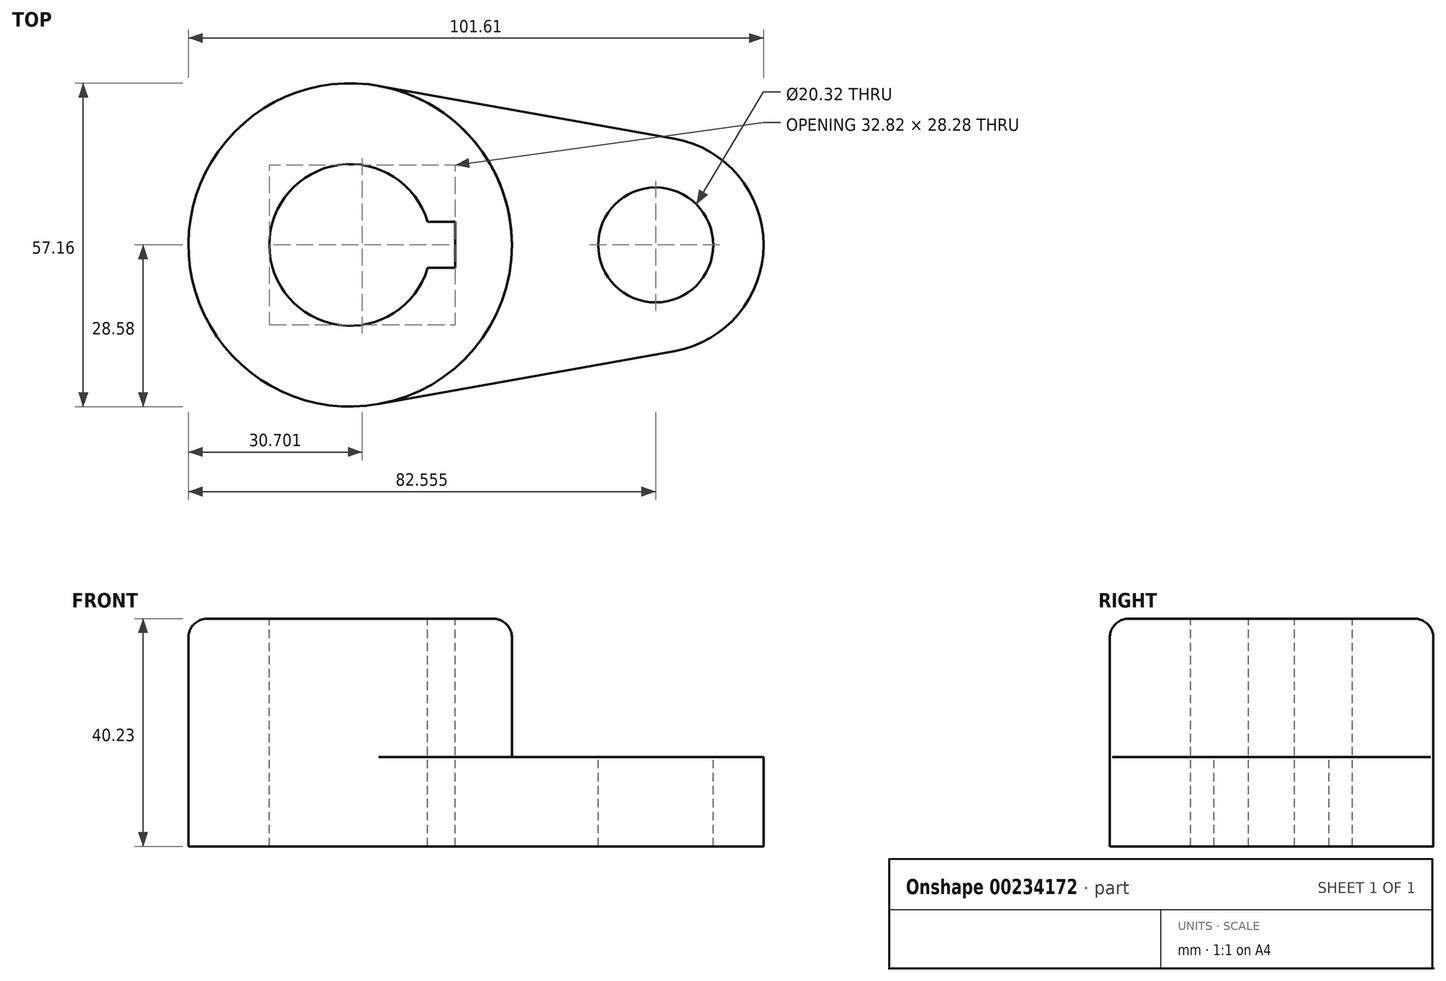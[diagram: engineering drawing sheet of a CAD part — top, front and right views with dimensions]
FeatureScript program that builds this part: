
annotation { "Feature Type Name" : "Feature", "Feature Type Description" : "" }
export const myFeature = defineFeature(function(context is Context, id is Id, definition is map)
    precondition{}
    {
        {
            var Q0;
            Q0=qCreatedBy(makeId("Top.planeOp"),FACE);
            var sketch = newSketch(context, id + "F0", { "sketchPlane" : qUnion([Q0])});
            skCircle(sketch, "E0", {"center": v(0, 0) * mm, "radius": 28.58 * mm});
            skSolve(sketch);
        }
        {
            var Q0;
            Q0=qSketchRegion(id+"F0",true);
            extrude(context, id + "F1", {"entities" : qUnion([Q0]), "depth" : 40.23 * mm});
        }
        {
            var Q0;
            Q0=qCreatedBy(makeId("Top.planeOp"),FACE);
            var sketch = newSketch(context, id + "F2", { "sketchPlane" : qUnion([Q0])});
            skLineSegment(sketch, "E1", {"start": v(53.98, 0) * mm, "end": v(53.98, -36.04) * mm, "construction": true});
            skLineSegment(sketch, "E2", {"start": v(53.98, -36.04) * mm, "end": v(53.98, 27.42) * mm, "construction": true});
            skArc(sketch, "E3", {"start": v(53.98, -19.05) * mm, "mid": v(73.03, 0) * mm, "end": v(53.98, 19.05) * mm});
            skLineSegment(sketch, "E4", {"start": v(5.04, -28.13) * mm, "end": v(57.34, -18.75) * mm});
            skArc(sketch, "E5", {"start": v(5.04, 28.13) * mm, "mid": v(-28.58, 0) * mm, "end": v(5.04, -28.13) * mm});
            skLineSegment(sketch, "E6", {"start": v(-19.16, 0) * mm, "end": v(100.57, 0) * mm, "construction": true});
            skLineSegment(sketch, "E7.MirrorCS", {"start": v(5.04, 28.13) * mm, "end": v(57.34, 18.75) * mm});
            skSolve(sketch);
        }
        {
            var Q0;
            Q0=qSketchRegion(id+"F2",true);
            extrude(context, id + "F3", {"entities" : qUnion([Q0]), "operationType" : NewBodyOperationType.ADD, "depth" : 15.77 * mm});
        }
        {
            var Q0;
            Q0=makeQuery(id+"F1.opExtrude","CAP_FACE",FACE,{"disambiguationData":[OSD([sQuery(id+"F0.wireOp",EDGE,"E0")])],"isStart":false});
            var sketch = newSketch(context, id + "F4", { "sketchPlane" : qUnion([Q0])});
            skLineSegment(sketch, "E8", {"start": v(-14.29, 0) * mm, "end": v(18.53, 0) * mm, "construction": true});
            skLineSegment(sketch, "E9", {"start": v(13.7, 4.06) * mm, "end": v(18.53, 4.06) * mm});
            skLineSegment(sketch, "E10", {"start": v(18.53, 4.06) * mm, "end": v(18.53, 0) * mm});
            skLineSegment(sketch, "E11.MirrorCS", {"start": v(13.7, -4.06) * mm, "end": v(18.53, -4.06) * mm});
            skLineSegment(sketch, "E12.MirrorCS", {"start": v(18.53, -4.06) * mm, "end": v(18.53, 0) * mm});
            skPoint(sketch, "E13.orphan", {"position": v(0, 4.06) * mm});
            skPoint(sketch, "E14.orphan", {"position": v(0, -4.06) * mm});
            skArc(sketch, "E15", {"start": v(13.7, 4.06) * mm, "mid": v(-14.29, 0) * mm, "end": v(13.7, -4.06) * mm});
            skSolve(sketch);
        }
        {
            var Q0;
            Q0=qSketchRegion(id+"F4",true);
            extrude(context, id + "F5", {"entities" : qUnion([Q0]), "operationType" : NewBodyOperationType.REMOVE, "endBound" : BoundingType.THROUGH_ALL, "oppositeDirection" : true, "depth" : 25.4 * mm});
        }
        {
            var Q0;
            Q0=makeQuery(id+"F3.opExtrude","CAP_FACE",FACE,{"disambiguationData":[OSD([sQuery(id+"F2.wireOp",EDGE,"E3"),sQuery(id+"F2.wireOp",EDGE,"E4"),sQuery(id+"F2.wireOp",EDGE,"E5"),sQuery(id+"F2.wireOp",EDGE,"E7.MirrorCS")])],"isStart":false});
            var sketch = newSketch(context, id + "F6", { "sketchPlane" : qUnion([Q0])});
            skCircle(sketch, "E16", {"center": v(53.98, 0) * mm, "radius": 10.16 * mm});
            skSolve(sketch);
        }
        {
            var Q0;
            Q0=qSketchRegion(id+"F6",true);
            extrude(context, id + "F7", {"entities" : qUnion([Q0]), "operationType" : NewBodyOperationType.REMOVE, "endBound" : BoundingType.THROUGH_ALL, "oppositeDirection" : true, "depth" : 25.4 * mm});
        }
        {
            var Q0;
            Q0=makeQuery(id+"F1.opExtrude","CAP_EDGE",EDGE,{"disambiguationData":[OSD([sQuery(id+"F0.wireOp",EDGE,"E0")])],"isStart":false});
            fillet(context, id + "F8", {"entities" : qUnion([Q0]), "radius" : 3.3 * mm, "tangentPropagation" : true, "allowEdgeOverflow" : false});
        }
    });
